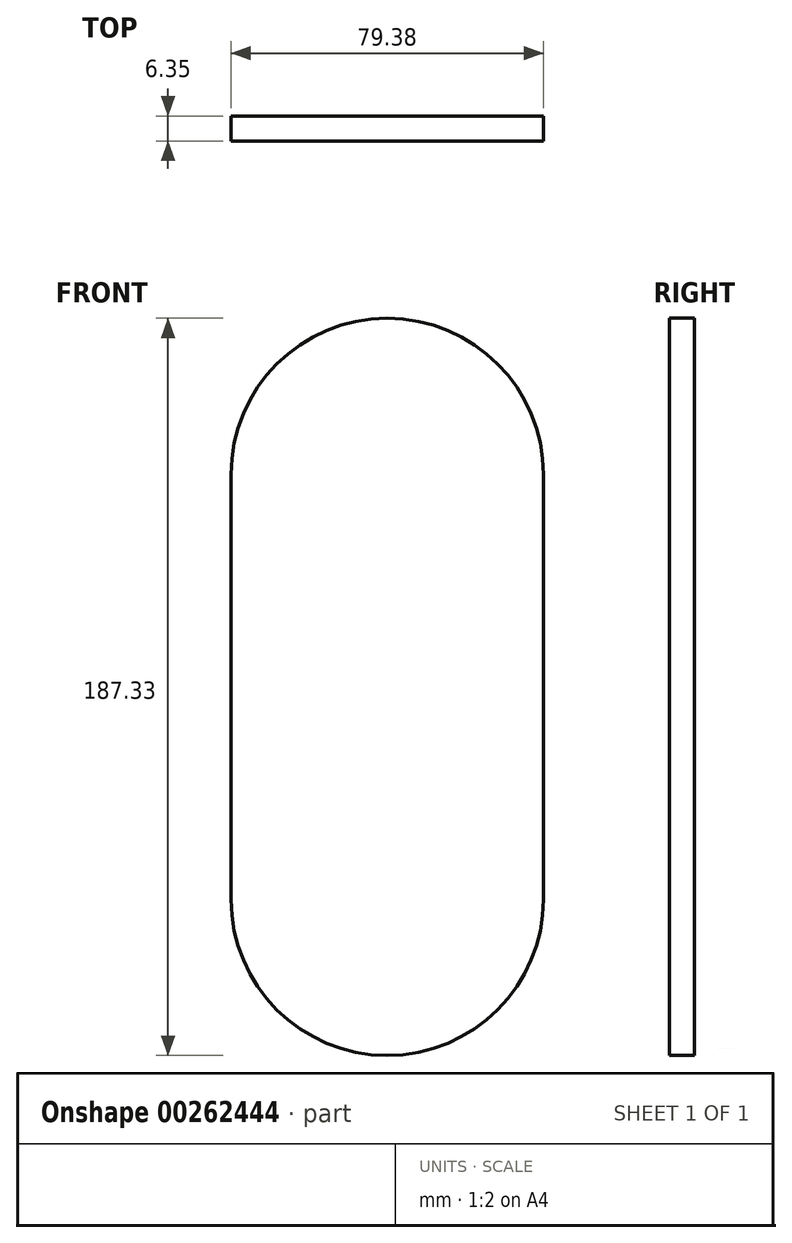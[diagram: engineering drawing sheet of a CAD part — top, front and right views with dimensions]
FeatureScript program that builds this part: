
annotation { "Feature Type Name" : "Feature", "Feature Type Description" : "" }
export const myFeature = defineFeature(function(context is Context, id is Id, definition is map)
    precondition{}
    {
        {
            var Q0;
            Q0=qCreatedBy(makeId("Front.planeOp"),FACE);
            var sketch = newSketch(context, id + "F0", { "sketchPlane" : qUnion([Q0])});
            skLineSegment(sketch, "E0", {"start": v(0, 32.52) * mm, "end": v(0, -75.43) * mm});
            skArc(sketch, "E1.0.startCap", {"start": v(-39.69, 32.52) * mm, "mid": v(0, 72.2) * mm, "end": v(39.69, 32.52) * mm});
            skArc(sketch, "E1.0.endCap", {"start": v(39.69, -75.43) * mm, "mid": v(0, -115.12) * mm, "end": v(-39.69, -75.43) * mm});
            skLineSegment(sketch, "E1.0.left", {"start": v(39.69, 32.52) * mm, "end": v(39.69, -75.43) * mm});
            skLineSegment(sketch, "E1.0.right", {"start": v(-39.69, 32.52) * mm, "end": v(-39.69, -75.43) * mm});
            skSolve(sketch);
        }
        {
            var Q0;
            Q0=qSketchRegion(id+"F0",true);
            extrude(context, id + "F1", {"entities" : qUnion([Q0]), "depth" : 6.35 * mm});
        }
    });
